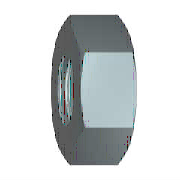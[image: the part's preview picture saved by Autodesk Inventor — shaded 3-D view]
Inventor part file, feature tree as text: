
AUTODESK INVENTOR PART (.ipt)
format: ipt  version: 2020 (Build 240168000, 168)  size: 165,888 bytes
history: native  units: mm (DEFAULTED — no unit token found)
features: sketch x3, chamfer x1, hole x1, other x1, plane x1
ambient origin geometry x7: Origin, YZ Plane, XZ Plane, X Axis, Y Axis, Z Axis, Center Point
bodies: Solid1 (feature_tree), Body (feature_tree)
feature tree (7):
  chamfer  "Chamfer1"  Angle=30.0deg  [1 undecoded]
  hole  "Thread"  [1 undecoded]
  other  "Work Axis1"
  plane  "Work Plane1"
  sketch  "Sketch1"  dims[d0=8.082904mm]
  sketch  "Sketch2"  dims[d1=3.2mm]
  sketch  "Sketch3"  dims[d2=0.0mm d3=30.0deg d4=30.0deg d5=5.8mm d6=5.8mm d7=90.0deg d25=3.242mm d26=6.0mm d27=4.0mm d28=2.0mm d29=14.3117mm d30=8.0mm d31=20.594885mm d8=0.378886mm d9=30.0deg d10=0.378886mm d11=30.0deg d13=0.0mm d14=0.0mm d39=0.0mm d40=0.378886mm d41=0.378886mm d42=0.0mm]
note: 2 required parameter values undecoded (feature->parameter linkage not recoverable at this tier; creation-order binding heuristic only, values carry confidence <= 0.55)
